# Revit family: WH458-FH-CSH
name_source: partatom
category: Plumbing Fixtures
revit_build: Autodesk Revit MEP 2016 (Build: 20150220_1215(x64)
units: mm (PartAtom-declared; Revit-internal decimal feet)

## family parameters
Cut with Voids When Loaded = No
Host = Face
OmniClass Number = 23.45.05.14.17
OmniClass Title = Showers
Part Type = Normal
Room Calculation Point = No
Round Connector Dimension = Use Diameter
Shared = Yes

## types (1)
- WH458-FH-CSH
    Assembly Code = D2010710
    CW Connection = Yes
    CWFU = 2
    Default Elevation = 55"
    Description = Surface Mount Ligature Resistant Wall Shower W/ Fixed Heads and Mounting Channel (Powder Coated White)
    HW Connection = Yes
    HWFU = 3
    Manufacturer = Whitehall Manufacturing Co.
    Material = Stainless Steel-Acorn-Type 304-Satin
    Model = WH458-FH-CSH
    Revised Date = 09/21/2015
    URL = https://www.whitehallmfg.com
    Vent Connection = No
    WFU = 4
    WH458-FH-CSH - Surface Mount Ligature W/ Wall Shower w/ Fixed Heads and Mounting Channel (Powder Coated White) = No
    Waste Connection = No

## geometry (parser evidence)
native form markers: Sweep x10
no freeform markers — native parametric forms only
